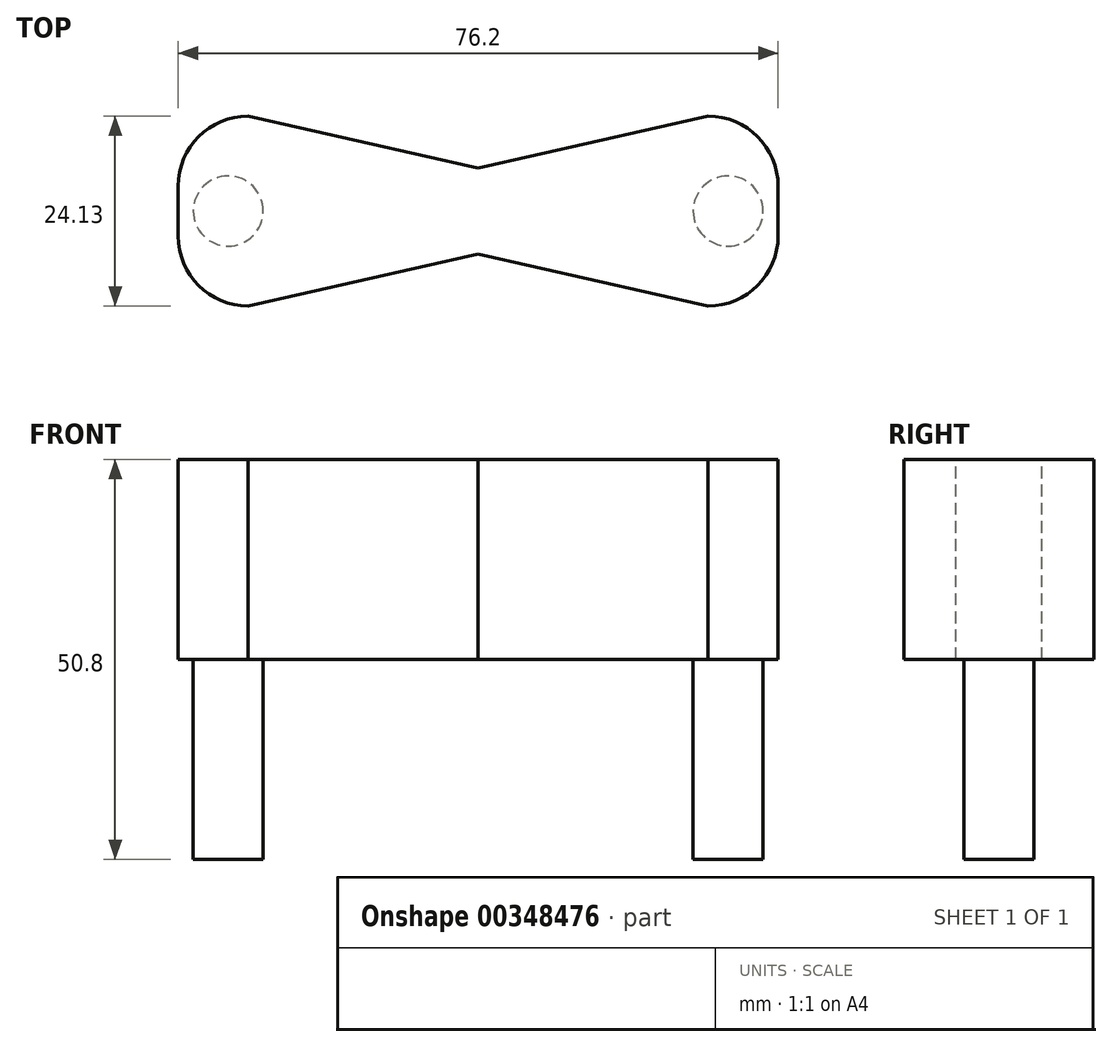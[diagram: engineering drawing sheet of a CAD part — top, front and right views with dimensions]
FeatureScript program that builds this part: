
annotation { "Feature Type Name" : "Feature", "Feature Type Description" : "" }
export const myFeature = defineFeature(function(context is Context, id is Id, definition is map)
    precondition{}
    {
        {
            var Q0;
            Q0=qCreatedBy(makeId("Top.planeOp"),FACE);
            var sketch = newSketch(context, id + "F0", { "sketchPlane" : qUnion([Q0])});
            skLineSegment(sketch, "E0.bottom", {"start": v(-41.49, 24.13) * mm, "end": v(34.71, 24.13) * mm});
            skLineSegment(sketch, "E0.top", {"start": v(-41.49, 0) * mm, "end": v(34.71, 0) * mm});
            skLineSegment(sketch, "E0.left", {"start": v(-41.49, 24.13) * mm, "end": v(-41.49, 0) * mm});
            skLineSegment(sketch, "E0.right", {"start": v(34.71, 24.13) * mm, "end": v(34.71, 0) * mm});
            skSolve(sketch);
        }
        {
            var Q0;
            Q0=makeQuery(id+"F0.imprint","IMPRINT",FACE,{"disambiguationData":[TD([[makeQuery(id+"F0.imprint","IMPRINT",EDGE,{"derivedFrom":sQuery(id+"F0.wireOp",EDGE,"E0.bottom")}),-1.0]])]});
            extrude(context, id + "F1", {"entities" : qUnion([Q0]), "depth" : 25.4 * mm});
        }
        {
            var Q0;
            Q0=makeQuery(id+"F1.opExtrude","SWEPT_EDGE",EDGE,{"disambiguationData":[OSD([sQuery(id+"F0.wireOp",EDGE,"E0.bottom"),sQuery(id+"F0.wireOp",EDGE,"E0.left")])]});
            var Q1;
            Q1=makeQuery(id+"F1.opExtrude","SWEPT_EDGE",EDGE,{"disambiguationData":[OSD([sQuery(id+"F0.wireOp",EDGE,"E0.bottom"),sQuery(id+"F0.wireOp",EDGE,"E0.right")])]});
            var Q2;
            Q2=makeQuery(id+"F1.opExtrude","SWEPT_EDGE",EDGE,{"disambiguationData":[OSD([sQuery(id+"F0.wireOp",EDGE,"E0.top"),sQuery(id+"F0.wireOp",EDGE,"E0.left")])]});
            var Q3;
            Q3=makeQuery(id+"F1.opExtrude","SWEPT_EDGE",EDGE,{"disambiguationData":[OSD([sQuery(id+"F0.wireOp",EDGE,"E0.top"),sQuery(id+"F0.wireOp",EDGE,"E0.right")])]});
            fillet(context, id + "F2", {"entities" : qUnion([Q0, Q1, Q2, Q3]), "radius" : 8.9 * mm, "tangentPropagation" : true, "allowEdgeOverflow" : false});
        }
        {
            var Q0;
            Q0=makeQuery(id+"F1.opExtrude","CAP_FACE",FACE,{"disambiguationData":[OSD([sQuery(id+"F0.wireOp",EDGE,"E0.bottom"),sQuery(id+"F0.wireOp",EDGE,"E0.top"),sQuery(id+"F0.wireOp",EDGE,"E0.left"),sQuery(id+"F0.wireOp",EDGE,"E0.right")])],"isStart":false});
            var sketch = newSketch(context, id + "F3", { "sketchPlane" : qUnion([Q0])});
            skLineSegment(sketch, "E1", {"start": v(-32.6, 24.13) * mm, "end": v(34.71, 8.89) * mm});
            skLineSegment(sketch, "E2", {"start": v(-41.49, 15.24) * mm, "end": v(25.82, 0) * mm});
            skLineSegment(sketch, "E3", {"start": v(-41.49, 8.89) * mm, "end": v(25.82, 24.13) * mm});
            skLineSegment(sketch, "E4", {"start": v(-32.6, 0) * mm, "end": v(34.71, 15.24) * mm});
            skSolve(sketch);
        }
        {
            var Q0;
            {var subQ1=sQuery(id+"F0.wireOp",EDGE,"E0.bottom");var subQ2=makeQuery(id+"F1.opExtrude","CAP_EDGE",EDGE,{"disambiguationData":[OSD([subQ1])],"isStart":false});Q0=makeQuery(id+"F3.imprint","IMPRINT",FACE,{"disambiguationData":[TD([[makeQuery(id+"F3.imprint","IMPRINT",EDGE,{"derivedFrom":subQ2}),-1.0]])]});}
            var Q1;
            {var subQ1=sQuery(id+"F0.wireOp",EDGE,"E0.top");var subQ2=makeQuery(id+"F1.opExtrude","CAP_EDGE",EDGE,{"disambiguationData":[OSD([subQ1])],"isStart":false});Q1=makeQuery(id+"F3.imprint","IMPRINT",FACE,{"disambiguationData":[TD([[makeQuery(id+"F3.imprint","IMPRINT",EDGE,{"derivedFrom":subQ2}),1.0]])]});}
            extrude(context, id + "F4", {"entities" : qUnion([Q0, Q1]), "operationType" : NewBodyOperationType.REMOVE, "oppositeDirection" : true, "depth" : 25.4 * mm});
        }
        {
            var Q0;
            Q0=makeQuery(id+"F1.opExtrude","CAP_FACE",FACE,{"disambiguationData":[OSD([sQuery(id+"F0.wireOp",EDGE,"E0.bottom"),sQuery(id+"F0.wireOp",EDGE,"E0.top"),sQuery(id+"F0.wireOp",EDGE,"E0.left"),sQuery(id+"F0.wireOp",EDGE,"E0.right")])],"isStart":true});
            var sketch = newSketch(context, id + "F5", { "sketchPlane" : qUnion([Q0])});
            skLineSegment(sketch, "E5", {"start": v(-41.49, -12.07) * mm, "end": v(-35.14, -12.07) * mm});
            skLineSegment(sketch, "E6", {"start": v(34.71, -12.07) * mm, "end": v(28.36, -12.07) * mm});
            skCircle(sketch, "E7", {"center": v(-35.14, -12.07) * mm, "radius": 4.45 * mm});
            skCircle(sketch, "E8", {"center": v(28.36, -12.07) * mm, "radius": 4.45 * mm});
            skSolve(sketch);
        }
        {
            var Q0;
            Q0=makeQuery(id+"F5.imprint","IMPRINT",FACE,{"disambiguationData":[TD([[makeQuery(id+"F5.imprint","IMPRINT",EDGE,{"derivedFrom":sQuery(id+"F5.wireOp",EDGE,"E7")}),1.0]])]});
            var Q1;
            Q1=makeQuery(id+"F5.imprint","IMPRINT",FACE,{"disambiguationData":[TD([[makeQuery(id+"F5.imprint","IMPRINT",EDGE,{"derivedFrom":sQuery(id+"F5.wireOp",EDGE,"E8")}),1.0]])]});
            extrude(context, id + "F6", {"entities" : qUnion([Q0, Q1]), "operationType" : NewBodyOperationType.ADD, "depth" : 25.4 * mm});
        }
    });
